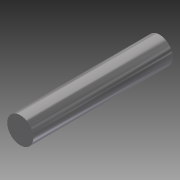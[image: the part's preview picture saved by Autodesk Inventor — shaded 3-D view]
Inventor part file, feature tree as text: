
AUTODESK INVENTOR PART (.ipt)
format: ipt  version: 2013 (Build 170138000, 138)  size: 75,264 bytes
history: native  units: in
note: dims shown in document units (in); Inventor stores cm internally (conversion verified against a paired STEP export)
features: extrude x1, sketch x1
ambient origin geometry x8: Origin, YZ Plane, XZ Plane, XY Plane, X Axis, Y Axis, Z Axis, Center Point
bodies: Solid1 (feature_tree)
feature tree (2):
  extrude  "Extrusion1"  Depth=2.0in TaperAngle=0.0deg
  sketch  "Sketch1"  dims[d0=0.375in d2=2.0in d3=0.0in]
